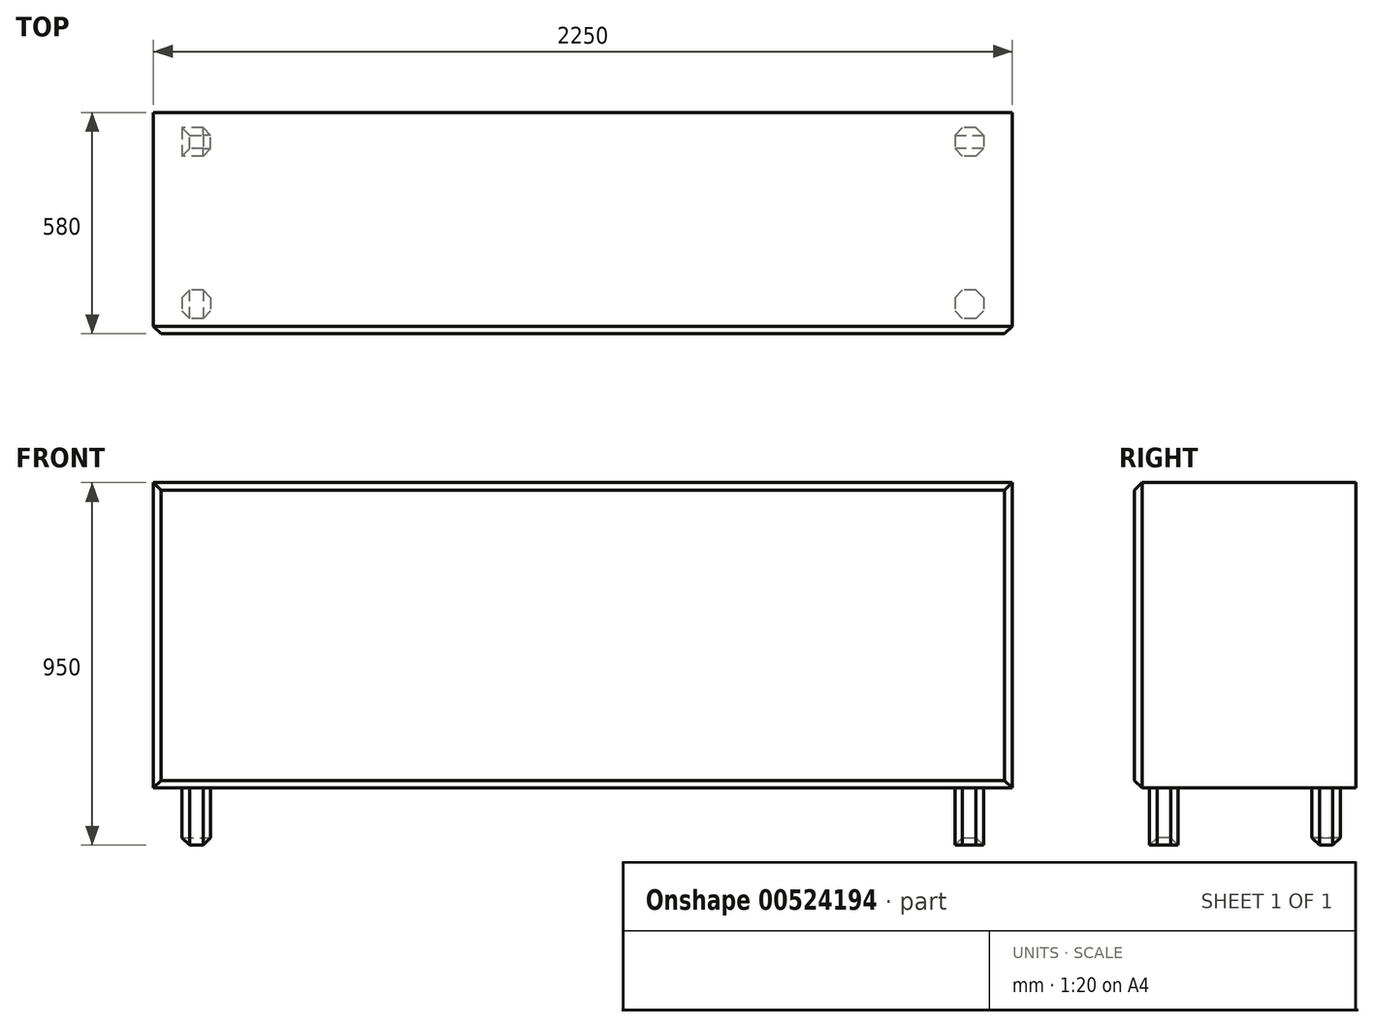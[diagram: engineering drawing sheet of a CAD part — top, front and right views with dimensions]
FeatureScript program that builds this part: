
annotation { "Feature Type Name" : "Feature", "Feature Type Description" : "" }
export const myFeature = defineFeature(function(context is Context, id is Id, definition is map)
    precondition{}
    {
        {
            var Q0;
            Q0=qCreatedBy(makeId("Top.planeOp"),FACE);
            var sketch = newSketch(context, id + "F0", { "sketchPlane" : qUnion([Q0])});
            skLineSegment(sketch, "E0.bottom", {"start": v(0, 0) * mm, "end": v(-2250, 0) * mm});
            skLineSegment(sketch, "E0.top", {"start": v(0, 580) * mm, "end": v(-2250, 580) * mm});
            skLineSegment(sketch, "E0.left", {"start": v(0, 0) * mm, "end": v(0, 580) * mm});
            skLineSegment(sketch, "E0.right", {"start": v(-2250, 0) * mm, "end": v(-2250, 580) * mm});
            skSolve(sketch);
        }
        {
            var Q0;
            Q0 = qSketchRegion(id + "F0", true);
            extrude(context, id + "F1", {"entities" : qUnion([Q0]), "depth" : 950 * mm, "offsetDistance" : 25 * mm});
        }
        {
            var Q0;
            Q0=makeQuery(id+"F1.opExtrude","SWEPT_FACE",FACE,{"disambiguationData":[OSD([sQuery(id+"F0.wireOp",EDGE,"E0.bottom")])]});
            var sketch = newSketch(context, id + "F2", { "sketchPlane" : qUnion([Q0])});
            skLineSegment(sketch, "E1.bottom", {"start": v(-2100, 0) * mm, "end": v(-150, 0) * mm});
            skLineSegment(sketch, "E1.top", {"start": v(-2100, 150) * mm, "end": v(-150, 150) * mm});
            skLineSegment(sketch, "E1.left", {"start": v(-2100, 0) * mm, "end": v(-2100, 150) * mm});
            skLineSegment(sketch, "E1.right", {"start": v(-150, 0) * mm, "end": v(-150, 150) * mm});
            skLineSegment(sketch, "E2.bottom", {"start": v(-2250, 0) * mm, "end": v(-2175, 0) * mm});
            skLineSegment(sketch, "E2.top", {"start": v(-2250, 150) * mm, "end": v(-2175, 150) * mm});
            skLineSegment(sketch, "E2.left", {"start": v(-2250, 0) * mm, "end": v(-2250, 150) * mm});
            skLineSegment(sketch, "E2.right", {"start": v(-2175, 0) * mm, "end": v(-2175, 150) * mm});
            skLineSegment(sketch, "E3.bottom", {"start": v(0, 0) * mm, "end": v(-75, 0) * mm});
            skLineSegment(sketch, "E3.top", {"start": v(0, 150) * mm, "end": v(-75, 150) * mm});
            skLineSegment(sketch, "E3.left", {"start": v(0, 0) * mm, "end": v(0, 150) * mm});
            skLineSegment(sketch, "E3.right", {"start": v(-75, 0) * mm, "end": v(-75, 150) * mm});
            skSolve(sketch);
        }
        {
            var Q0;
            Q0 = qSketchRegion(id + "F2", true);
            extrude(context, id + "F3", {"entities" : qUnion([Q0]), "operationType" : NewBodyOperationType.REMOVE, "oppositeDirection" : true, "depth" : 600 * mm, "offsetDistance" : 25 * mm});
        }
        {
            var Q0;
            Q0=makeQuery(id+"F3.boolean.opBoolean","COPY",FACE,{"derivedFrom":makeQuery(id+"F3.opExtrude","SWEPT_FACE",FACE,{"disambiguationData":[OSD([sQuery(id+"F2.wireOp",EDGE,"E2.right")])]})});
            var sketch = newSketch(context, id + "F4", { "sketchPlane" : qUnion([Q0])});
            skLineSegment(sketch, "E4.bottom", {"start": v(-580, 150) * mm, "end": v(-540, 150) * mm});
            skLineSegment(sketch, "E4.top", {"start": v(-580, 0) * mm, "end": v(-540, 0) * mm});
            skLineSegment(sketch, "E4.left", {"start": v(-580, 150) * mm, "end": v(-580, 0) * mm});
            skLineSegment(sketch, "E4.right", {"start": v(-540, 150) * mm, "end": v(-540, 0) * mm});
            skLineSegment(sketch, "E5.bottom", {"start": v(0, 150) * mm, "end": v(-40, 150) * mm});
            skLineSegment(sketch, "E5.top", {"start": v(0, 0) * mm, "end": v(-40, 0) * mm});
            skLineSegment(sketch, "E5.left", {"start": v(0, 150) * mm, "end": v(0, 0) * mm});
            skLineSegment(sketch, "E5.right", {"start": v(-40, 150) * mm, "end": v(-40, 0) * mm});
            skLineSegment(sketch, "E6.bottom", {"start": v(-465, 0) * mm, "end": v(-115, 0) * mm});
            skLineSegment(sketch, "E6.top", {"start": v(-465, 150) * mm, "end": v(-115, 150) * mm});
            skLineSegment(sketch, "E6.left", {"start": v(-465, 0) * mm, "end": v(-465, 150) * mm});
            skLineSegment(sketch, "E6.right", {"start": v(-115, 0) * mm, "end": v(-115, 150) * mm});
            skSolve(sketch);
        }
        {
            var Q0;
            Q0 = qSketchRegion(id + "F4", true);
            extrude(context, id + "F5", {"entities" : qUnion([Q0]), "operationType" : NewBodyOperationType.REMOVE, "oppositeDirection" : true, "depth" : 2250 * mm, "offsetDistance" : 25 * mm});
        }
        {
            var Q0;
            Q0=makeQuery(id+"F1.opExtrude","SWEPT_FACE",FACE,{"disambiguationData":[OSD([sQuery(id+"F0.wireOp",EDGE,"E0.bottom")])]});
            var Q1;
            Q1=makeQuery(id+"F5.boolean.opBoolean","COPY",EDGE,{"derivedFrom":makeQuery(id+"F5.opExtrude","CAP_EDGE",EDGE,{"disambiguationData":[OSD([sQuery(id+"F4.wireOp",EDGE,"E5.right")])],"isStart":true})});
            var Q2;
            Q2=makeQuery(id+"F5.boolean.opBoolean","INTERSECT",EDGE,{"derivedFrom":[makeQuery(id+"F3.boolean.opBoolean","COPY",FACE,{"derivedFrom":makeQuery(id+"F3.opExtrude","SWEPT_FACE",FACE,{"disambiguationData":[OSD([sQuery(id+"F2.wireOp",EDGE,"E1.left")])]})}),makeQuery(id+"F5.opExtrude","SWEPT_FACE",FACE,{"disambiguationData":[OSD([sQuery(id+"F4.wireOp",EDGE,"E5.right")])]})]});
            var Q3;
            Q3=makeQuery(id+"F5.boolean.opBoolean","INTERSECT",EDGE,{"derivedFrom":[makeQuery(id+"F3.boolean.opBoolean","COPY",FACE,{"derivedFrom":makeQuery(id+"F3.opExtrude","SWEPT_FACE",FACE,{"disambiguationData":[OSD([sQuery(id+"F2.wireOp",EDGE,"E1.left")])]})}),makeQuery(id+"F5.opExtrude","SWEPT_FACE",FACE,{"disambiguationData":[OSD([sQuery(id+"F4.wireOp",EDGE,"E6.right")])]})]});
            var Q4;
            Q4=makeQuery(id+"F5.boolean.opBoolean","COPY",EDGE,{"derivedFrom":makeQuery(id+"F5.opExtrude","CAP_EDGE",EDGE,{"disambiguationData":[OSD([sQuery(id+"F4.wireOp",EDGE,"E6.left")])],"isStart":true})});
            var Q5;
            Q5=makeQuery(id+"F5.boolean.opBoolean","INTERSECT",EDGE,{"derivedFrom":[makeQuery(id+"F3.boolean.opBoolean","COPY",FACE,{"derivedFrom":makeQuery(id+"F3.opExtrude","SWEPT_FACE",FACE,{"disambiguationData":[OSD([sQuery(id+"F2.wireOp",EDGE,"E1.left")])]})}),makeQuery(id+"F5.opExtrude","SWEPT_FACE",FACE,{"disambiguationData":[OSD([sQuery(id+"F4.wireOp",EDGE,"E6.left")])]})]});
            var Q6;
            Q6=makeQuery(id+"F5.boolean.opBoolean","INTERSECT",EDGE,{"derivedFrom":[makeQuery(id+"F3.boolean.opBoolean","COPY",FACE,{"derivedFrom":makeQuery(id+"F3.opExtrude","SWEPT_FACE",FACE,{"disambiguationData":[OSD([sQuery(id+"F2.wireOp",EDGE,"E1.left")])]})}),makeQuery(id+"F5.opExtrude","SWEPT_FACE",FACE,{"disambiguationData":[OSD([sQuery(id+"F4.wireOp",EDGE,"E4.right")])]})]});
            var Q7;
            Q7=makeQuery(id+"F5.boolean.opBoolean","COPY",EDGE,{"derivedFrom":makeQuery(id+"F5.opExtrude","CAP_EDGE",EDGE,{"disambiguationData":[OSD([sQuery(id+"F4.wireOp",EDGE,"E4.right")])],"isStart":true})});
            var Q8;
            Q8=makeQuery(id+"F5.boolean.opBoolean","COPY",EDGE,{"derivedFrom":makeQuery(id+"F5.opExtrude","CAP_EDGE",EDGE,{"disambiguationData":[OSD([sQuery(id+"F4.wireOp",EDGE,"E6.right")])],"isStart":true})});
            var Q9;
            Q9=makeQuery(id+"F5.boolean.opBoolean","INTERSECT",EDGE,{"derivedFrom":[makeQuery(id+"F3.boolean.opBoolean","COPY",FACE,{"derivedFrom":makeQuery(id+"F3.opExtrude","SWEPT_FACE",FACE,{"disambiguationData":[OSD([sQuery(id+"F2.wireOp",EDGE,"E3.right")])]})}),makeQuery(id+"F5.opExtrude","SWEPT_FACE",FACE,{"disambiguationData":[OSD([sQuery(id+"F4.wireOp",EDGE,"E4.right")])]})]});
            var Q10;
            Q10=makeQuery(id+"F5.boolean.opBoolean","INTERSECT",EDGE,{"derivedFrom":[makeQuery(id+"F3.boolean.opBoolean","COPY",FACE,{"derivedFrom":makeQuery(id+"F3.opExtrude","SWEPT_FACE",FACE,{"disambiguationData":[OSD([sQuery(id+"F2.wireOp",EDGE,"E3.right")])]})}),makeQuery(id+"F5.opExtrude","SWEPT_FACE",FACE,{"disambiguationData":[OSD([sQuery(id+"F4.wireOp",EDGE,"E6.left")])]})]});
            var Q11;
            Q11=makeQuery(id+"F5.boolean.opBoolean","INTERSECT",EDGE,{"derivedFrom":[makeQuery(id+"F3.boolean.opBoolean","COPY",FACE,{"derivedFrom":makeQuery(id+"F3.opExtrude","SWEPT_FACE",FACE,{"disambiguationData":[OSD([sQuery(id+"F2.wireOp",EDGE,"E3.right")])]})}),makeQuery(id+"F5.opExtrude","SWEPT_FACE",FACE,{"disambiguationData":[OSD([sQuery(id+"F4.wireOp",EDGE,"E6.right")])]})]});
            var Q12;
            Q12=makeQuery(id+"F5.boolean.opBoolean","INTERSECT",EDGE,{"derivedFrom":[makeQuery(id+"F3.boolean.opBoolean","COPY",FACE,{"derivedFrom":makeQuery(id+"F3.opExtrude","SWEPT_FACE",FACE,{"disambiguationData":[OSD([sQuery(id+"F2.wireOp",EDGE,"E3.right")])]})}),makeQuery(id+"F5.opExtrude","SWEPT_FACE",FACE,{"disambiguationData":[OSD([sQuery(id+"F4.wireOp",EDGE,"E5.right")])]})]});
            var Q13;
            Q13=makeQuery(id+"F5.boolean.opBoolean","INTERSECT",EDGE,{"derivedFrom":[makeQuery(id+"F3.boolean.opBoolean","COPY",FACE,{"derivedFrom":makeQuery(id+"F3.opExtrude","SWEPT_FACE",FACE,{"disambiguationData":[OSD([sQuery(id+"F2.wireOp",EDGE,"E1.right")])]})}),makeQuery(id+"F5.opExtrude","SWEPT_FACE",FACE,{"disambiguationData":[OSD([sQuery(id+"F4.wireOp",EDGE,"E6.left")])]})]});
            var Q14;
            Q14=makeQuery(id+"F5.boolean.opBoolean","INTERSECT",EDGE,{"derivedFrom":[makeQuery(id+"F3.boolean.opBoolean","COPY",FACE,{"derivedFrom":makeQuery(id+"F3.opExtrude","SWEPT_FACE",FACE,{"disambiguationData":[OSD([sQuery(id+"F2.wireOp",EDGE,"E1.right")])]})}),makeQuery(id+"F5.opExtrude","SWEPT_FACE",FACE,{"disambiguationData":[OSD([sQuery(id+"F4.wireOp",EDGE,"E4.right")])]})]});
            var Q15;
            Q15=makeQuery(id+"F5.boolean.opBoolean","INTERSECT",EDGE,{"derivedFrom":[makeQuery(id+"F3.boolean.opBoolean","COPY",FACE,{"derivedFrom":makeQuery(id+"F3.opExtrude","SWEPT_FACE",FACE,{"disambiguationData":[OSD([sQuery(id+"F2.wireOp",EDGE,"E1.right")])]})}),makeQuery(id+"F5.opExtrude","SWEPT_FACE",FACE,{"disambiguationData":[OSD([sQuery(id+"F4.wireOp",EDGE,"E6.right")])]})]});
            var Q16;
            Q16=makeQuery(id+"F5.boolean.opBoolean","INTERSECT",EDGE,{"derivedFrom":[makeQuery(id+"F3.boolean.opBoolean","COPY",FACE,{"derivedFrom":makeQuery(id+"F3.opExtrude","SWEPT_FACE",FACE,{"disambiguationData":[OSD([sQuery(id+"F2.wireOp",EDGE,"E1.right")])]})}),makeQuery(id+"F5.opExtrude","SWEPT_FACE",FACE,{"disambiguationData":[OSD([sQuery(id+"F4.wireOp",EDGE,"E5.right")])]})]});
            var Q17;
            {var subQ0=sQuery(id+"F0.wireOp",EDGE,"E0.bottom");var subQ1=sQuery(id+"F4.wireOp",EDGE,"E5.right");Q17=makeQuery(id+"F5.boolean.opBoolean","COPY",EDGE,{"disambiguationData":[TD([makeQuery(id+"F3.boolean.opBoolean","COPY",FACE,{"derivedFrom":makeQuery(id+"F3.opExtrude","SWEPT_FACE",FACE,{"disambiguationData":[OSD([sQuery(id+"F2.wireOp",EDGE,"E1.right")])]})})])],"derivedFrom":makeQuery(id+"F5.opExtrude","SWEPT_EDGE",EDGE,{"disambiguationData":[OSD([subQ0,sQuery(id+"F2.wireOp",EDGE,"E2.bottom"),sQuery(id+"F2.wireOp",EDGE,"E2.right"),sQuery(id+"F4.wireOp",EDGE,"E5.top"),subQ1])]})});}
            var Q18;
            {var subQ0=sQuery(id+"F0.wireOp",EDGE,"E0.bottom");var subQ1=sQuery(id+"F2.wireOp",EDGE,"E3.right");Q18=makeQuery(id+"F5.boolean.opBoolean","SPLIT",EDGE,{"disambiguationData":[TD([makeQuery(id+"F5.opExtrude","SWEPT_FACE",FACE,{"disambiguationData":[OSD([sQuery(id+"F4.wireOp",EDGE,"E5.right")])]})])],"derivedFrom":makeQuery(id+"F3.boolean.opBoolean","COPY",EDGE,{"derivedFrom":makeQuery(id+"F3.opExtrude","SWEPT_EDGE",EDGE,{"disambiguationData":[OSD([subQ0,sQuery(id+"F2.wireOp",EDGE,"E3.bottom"),subQ1])]})})});}
            var Q19;
            {var subQ0=sQuery(id+"F0.wireOp",EDGE,"E0.bottom");var subQ1=sQuery(id+"F4.wireOp",EDGE,"E6.right");Q19=makeQuery(id+"F5.boolean.opBoolean","COPY",EDGE,{"disambiguationData":[TD([makeQuery(id+"F3.boolean.opBoolean","COPY",FACE,{"derivedFrom":makeQuery(id+"F3.opExtrude","SWEPT_FACE",FACE,{"disambiguationData":[OSD([sQuery(id+"F2.wireOp",EDGE,"E1.right")])]})})])],"derivedFrom":makeQuery(id+"F5.opExtrude","SWEPT_EDGE",EDGE,{"disambiguationData":[OSD([subQ0,sQuery(id+"F2.wireOp",EDGE,"E2.bottom"),sQuery(id+"F2.wireOp",EDGE,"E2.right"),sQuery(id+"F4.wireOp",EDGE,"E6.bottom"),subQ1])]})});}
            var Q20;
            {var subQ0=sQuery(id+"F0.wireOp",EDGE,"E0.bottom");var subQ1=sQuery(id+"F2.wireOp",EDGE,"E1.right");Q20=makeQuery(id+"F5.boolean.opBoolean","SPLIT",EDGE,{"disambiguationData":[TD([makeQuery(id+"F5.opExtrude","SWEPT_FACE",FACE,{"disambiguationData":[OSD([sQuery(id+"F4.wireOp",EDGE,"E5.right")])]})])],"derivedFrom":makeQuery(id+"F3.boolean.opBoolean","COPY",EDGE,{"derivedFrom":makeQuery(id+"F3.opExtrude","SWEPT_EDGE",EDGE,{"disambiguationData":[OSD([subQ0,sQuery(id+"F2.wireOp",EDGE,"E1.bottom"),subQ1])]})})});}
            var Q21;
            {var subQ0=sQuery(id+"F0.wireOp",EDGE,"E0.bottom");var subQ1=sQuery(id+"F4.wireOp",EDGE,"E6.left");Q21=makeQuery(id+"F5.boolean.opBoolean","COPY",EDGE,{"disambiguationData":[TD([makeQuery(id+"F3.boolean.opBoolean","COPY",FACE,{"derivedFrom":makeQuery(id+"F3.opExtrude","SWEPT_FACE",FACE,{"disambiguationData":[OSD([sQuery(id+"F2.wireOp",EDGE,"E1.right")])]})})])],"derivedFrom":makeQuery(id+"F5.opExtrude","SWEPT_EDGE",EDGE,{"disambiguationData":[OSD([subQ0,sQuery(id+"F2.wireOp",EDGE,"E2.bottom"),sQuery(id+"F2.wireOp",EDGE,"E2.right"),sQuery(id+"F4.wireOp",EDGE,"E6.bottom"),subQ1])]})});}
            var Q22;
            {var subQ0=sQuery(id+"F0.wireOp",EDGE,"E0.bottom");var subQ1=sQuery(id+"F2.wireOp",EDGE,"E3.right");Q22=makeQuery(id+"F5.boolean.opBoolean","SPLIT",EDGE,{"disambiguationData":[TD([makeQuery(id+"F5.opExtrude","SWEPT_FACE",FACE,{"disambiguationData":[OSD([sQuery(id+"F4.wireOp",EDGE,"E4.right")])]})])],"derivedFrom":makeQuery(id+"F3.boolean.opBoolean","COPY",EDGE,{"derivedFrom":makeQuery(id+"F3.opExtrude","SWEPT_EDGE",EDGE,{"disambiguationData":[OSD([subQ0,sQuery(id+"F2.wireOp",EDGE,"E3.bottom"),subQ1])]})})});}
            var Q23;
            {var subQ0=sQuery(id+"F0.wireOp",EDGE,"E0.bottom");var subQ1=sQuery(id+"F4.wireOp",EDGE,"E4.right");Q23=makeQuery(id+"F5.boolean.opBoolean","COPY",EDGE,{"disambiguationData":[TD([makeQuery(id+"F3.boolean.opBoolean","COPY",FACE,{"derivedFrom":makeQuery(id+"F3.opExtrude","SWEPT_FACE",FACE,{"disambiguationData":[OSD([sQuery(id+"F2.wireOp",EDGE,"E1.right")])]})})])],"derivedFrom":makeQuery(id+"F5.opExtrude","SWEPT_EDGE",EDGE,{"disambiguationData":[OSD([subQ0,sQuery(id+"F2.wireOp",EDGE,"E2.bottom"),sQuery(id+"F2.wireOp",EDGE,"E2.right"),sQuery(id+"F4.wireOp",EDGE,"E4.top"),subQ1])]})});}
            var Q24;
            {var subQ0=sQuery(id+"F0.wireOp",EDGE,"E0.bottom");var subQ1=sQuery(id+"F2.wireOp",EDGE,"E1.right");Q24=makeQuery(id+"F5.boolean.opBoolean","SPLIT",EDGE,{"disambiguationData":[TD([makeQuery(id+"F5.opExtrude","SWEPT_FACE",FACE,{"disambiguationData":[OSD([sQuery(id+"F4.wireOp",EDGE,"E4.right")])]})])],"derivedFrom":makeQuery(id+"F3.boolean.opBoolean","COPY",EDGE,{"derivedFrom":makeQuery(id+"F3.opExtrude","SWEPT_EDGE",EDGE,{"disambiguationData":[OSD([subQ0,sQuery(id+"F2.wireOp",EDGE,"E1.bottom"),subQ1])]})})});}
            var Q25;
            {var subQ0=sQuery(id+"F0.wireOp",EDGE,"E0.bottom");var subQ1=sQuery(id+"F2.wireOp",EDGE,"E2.right");var subQ2=sQuery(id+"F4.wireOp",EDGE,"E6.left");Q25=makeQuery(id+"F5.boolean.opBoolean","COPY",EDGE,{"disambiguationData":[TD([makeQuery(id+"F3.boolean.opBoolean","COPY",FACE,{"derivedFrom":makeQuery(id+"F3.opExtrude","SWEPT_FACE",FACE,{"disambiguationData":[OSD([sQuery(id+"F2.wireOp",EDGE,"E1.left")])]})})])],"derivedFrom":makeQuery(id+"F5.opExtrude","SWEPT_EDGE",EDGE,{"disambiguationData":[OSD([subQ0,sQuery(id+"F2.wireOp",EDGE,"E2.bottom"),subQ1,sQuery(id+"F4.wireOp",EDGE,"E6.bottom"),subQ2])]})});}
            var Q26;
            {var subQ0=sQuery(id+"F0.wireOp",EDGE,"E0.bottom");var subQ1=sQuery(id+"F2.wireOp",EDGE,"E2.right");Q26=makeQuery(id+"F5.boolean.opBoolean","SPLIT",EDGE,{"disambiguationData":[TD([makeQuery(id+"F5.opExtrude","SWEPT_FACE",FACE,{"disambiguationData":[OSD([sQuery(id+"F4.wireOp",EDGE,"E4.right")])]})])],"derivedFrom":makeQuery(id+"F3.boolean.opBoolean","COPY",EDGE,{"derivedFrom":makeQuery(id+"F3.opExtrude","SWEPT_EDGE",EDGE,{"disambiguationData":[OSD([subQ0,sQuery(id+"F2.wireOp",EDGE,"E2.bottom"),subQ1])]})})});}
            var Q27;
            {var subQ0=sQuery(id+"F0.wireOp",EDGE,"E0.bottom");var subQ1=sQuery(id+"F2.wireOp",EDGE,"E2.right");var subQ2=sQuery(id+"F4.wireOp",EDGE,"E4.right");Q27=makeQuery(id+"F5.boolean.opBoolean","COPY",EDGE,{"disambiguationData":[TD([makeQuery(id+"F3.boolean.opBoolean","COPY",FACE,{"derivedFrom":makeQuery(id+"F3.opExtrude","SWEPT_FACE",FACE,{"disambiguationData":[OSD([sQuery(id+"F2.wireOp",EDGE,"E1.left")])]})})])],"derivedFrom":makeQuery(id+"F5.opExtrude","SWEPT_EDGE",EDGE,{"disambiguationData":[OSD([subQ0,sQuery(id+"F2.wireOp",EDGE,"E2.bottom"),subQ1,sQuery(id+"F4.wireOp",EDGE,"E4.top"),subQ2])]})});}
            var Q28;
            {var subQ0=sQuery(id+"F0.wireOp",EDGE,"E0.bottom");var subQ1=sQuery(id+"F2.wireOp",EDGE,"E1.left");Q28=makeQuery(id+"F5.boolean.opBoolean","SPLIT",EDGE,{"disambiguationData":[TD([makeQuery(id+"F5.opExtrude","SWEPT_FACE",FACE,{"disambiguationData":[OSD([sQuery(id+"F4.wireOp",EDGE,"E4.right")])]})])],"derivedFrom":makeQuery(id+"F3.boolean.opBoolean","COPY",EDGE,{"derivedFrom":makeQuery(id+"F3.opExtrude","SWEPT_EDGE",EDGE,{"disambiguationData":[OSD([subQ0,sQuery(id+"F2.wireOp",EDGE,"E1.bottom"),subQ1])]})})});}
            var Q29;
            {var subQ0=sQuery(id+"F0.wireOp",EDGE,"E0.bottom");var subQ1=sQuery(id+"F2.wireOp",EDGE,"E2.right");var subQ2=sQuery(id+"F4.wireOp",EDGE,"E6.right");Q29=makeQuery(id+"F5.boolean.opBoolean","COPY",EDGE,{"disambiguationData":[TD([makeQuery(id+"F3.boolean.opBoolean","COPY",FACE,{"derivedFrom":makeQuery(id+"F3.opExtrude","SWEPT_FACE",FACE,{"disambiguationData":[OSD([sQuery(id+"F2.wireOp",EDGE,"E1.left")])]})})])],"derivedFrom":makeQuery(id+"F5.opExtrude","SWEPT_EDGE",EDGE,{"disambiguationData":[OSD([subQ0,sQuery(id+"F2.wireOp",EDGE,"E2.bottom"),subQ1,sQuery(id+"F4.wireOp",EDGE,"E6.bottom"),subQ2])]})});}
            var Q30;
            {var subQ0=sQuery(id+"F0.wireOp",EDGE,"E0.bottom");var subQ1=sQuery(id+"F2.wireOp",EDGE,"E2.right");var subQ2=sQuery(id+"F4.wireOp",EDGE,"E5.right");Q30=makeQuery(id+"F5.boolean.opBoolean","COPY",EDGE,{"disambiguationData":[TD([makeQuery(id+"F3.boolean.opBoolean","COPY",FACE,{"derivedFrom":makeQuery(id+"F3.opExtrude","SWEPT_FACE",FACE,{"disambiguationData":[OSD([sQuery(id+"F2.wireOp",EDGE,"E1.left")])]})})])],"derivedFrom":makeQuery(id+"F5.opExtrude","SWEPT_EDGE",EDGE,{"disambiguationData":[OSD([subQ0,sQuery(id+"F2.wireOp",EDGE,"E2.bottom"),subQ1,sQuery(id+"F4.wireOp",EDGE,"E5.top"),subQ2])]})});}
            var Q31;
            {var subQ0=sQuery(id+"F0.wireOp",EDGE,"E0.bottom");var subQ1=sQuery(id+"F2.wireOp",EDGE,"E1.left");Q31=makeQuery(id+"F5.boolean.opBoolean","SPLIT",EDGE,{"disambiguationData":[TD([makeQuery(id+"F5.opExtrude","SWEPT_FACE",FACE,{"disambiguationData":[OSD([sQuery(id+"F4.wireOp",EDGE,"E5.right")])]})])],"derivedFrom":makeQuery(id+"F3.boolean.opBoolean","COPY",EDGE,{"derivedFrom":makeQuery(id+"F3.opExtrude","SWEPT_EDGE",EDGE,{"disambiguationData":[OSD([subQ0,sQuery(id+"F2.wireOp",EDGE,"E1.bottom"),subQ1])]})})});}
            var Q32;
            {var subQ0=sQuery(id+"F0.wireOp",EDGE,"E0.bottom");var subQ1=sQuery(id+"F2.wireOp",EDGE,"E2.right");Q32=makeQuery(id+"F5.boolean.opBoolean","SPLIT",EDGE,{"disambiguationData":[TD([makeQuery(id+"F5.opExtrude","SWEPT_FACE",FACE,{"disambiguationData":[OSD([sQuery(id+"F4.wireOp",EDGE,"E5.right")])]})])],"derivedFrom":makeQuery(id+"F3.boolean.opBoolean","COPY",EDGE,{"derivedFrom":makeQuery(id+"F3.opExtrude","SWEPT_EDGE",EDGE,{"disambiguationData":[OSD([subQ0,sQuery(id+"F2.wireOp",EDGE,"E2.bottom"),subQ1])]})})});}
            chamfer(context, id + "F6", {"entities" : qUnion([Q0, Q1, Q2, Q3, Q4, Q5, Q6, Q7, Q8, Q9, Q10, Q11, Q12, Q13, Q14, Q15, Q16, Q17, Q18, Q19, Q20, Q21, Q22, Q23, Q24, Q25, Q26, Q27, Q28, Q29, Q30, Q31, Q32]), "width" : 20 * mm, "tangentPropagation" : true});
        }
    });
